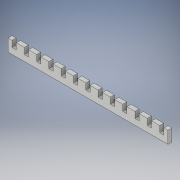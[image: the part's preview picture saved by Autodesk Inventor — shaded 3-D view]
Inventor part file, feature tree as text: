
AUTODESK INVENTOR PART (.ipt)
format: ipt  version: 2017 (Build 210142000, 142)  size: 166,912 bytes
history: native  units: in
note: dims shown in document units (in); Inventor stores cm internally (conversion verified against a paired STEP export)
features: mirror x6, plane x2, extrude x1, sketch x1
ambient origin geometry x8: Origin, YZ Plane, XZ Plane, XY Plane, X Axis, Y Axis, Z Axis, Center Point
bodies: Solid1 (feature_tree)
feature tree (10):
  extrude  "Extrusion1"  Depth=0.2047in
  mirror  "Mirror1"
  mirror  "Mirror2"
  mirror  "Mirror3"
  mirror  "Mirror4"
  mirror  "Mirror5"
  plane  "Work Plane1"
  mirror  "Mirror6"
  sketch  "Sketch1"  dims[d0=0.5906in d1=0.2047in d2=0.1969in d3=0.1969in d4=0.2953in d5=0.1969in d6=0.0in]
  plane  "Work Plane2"
